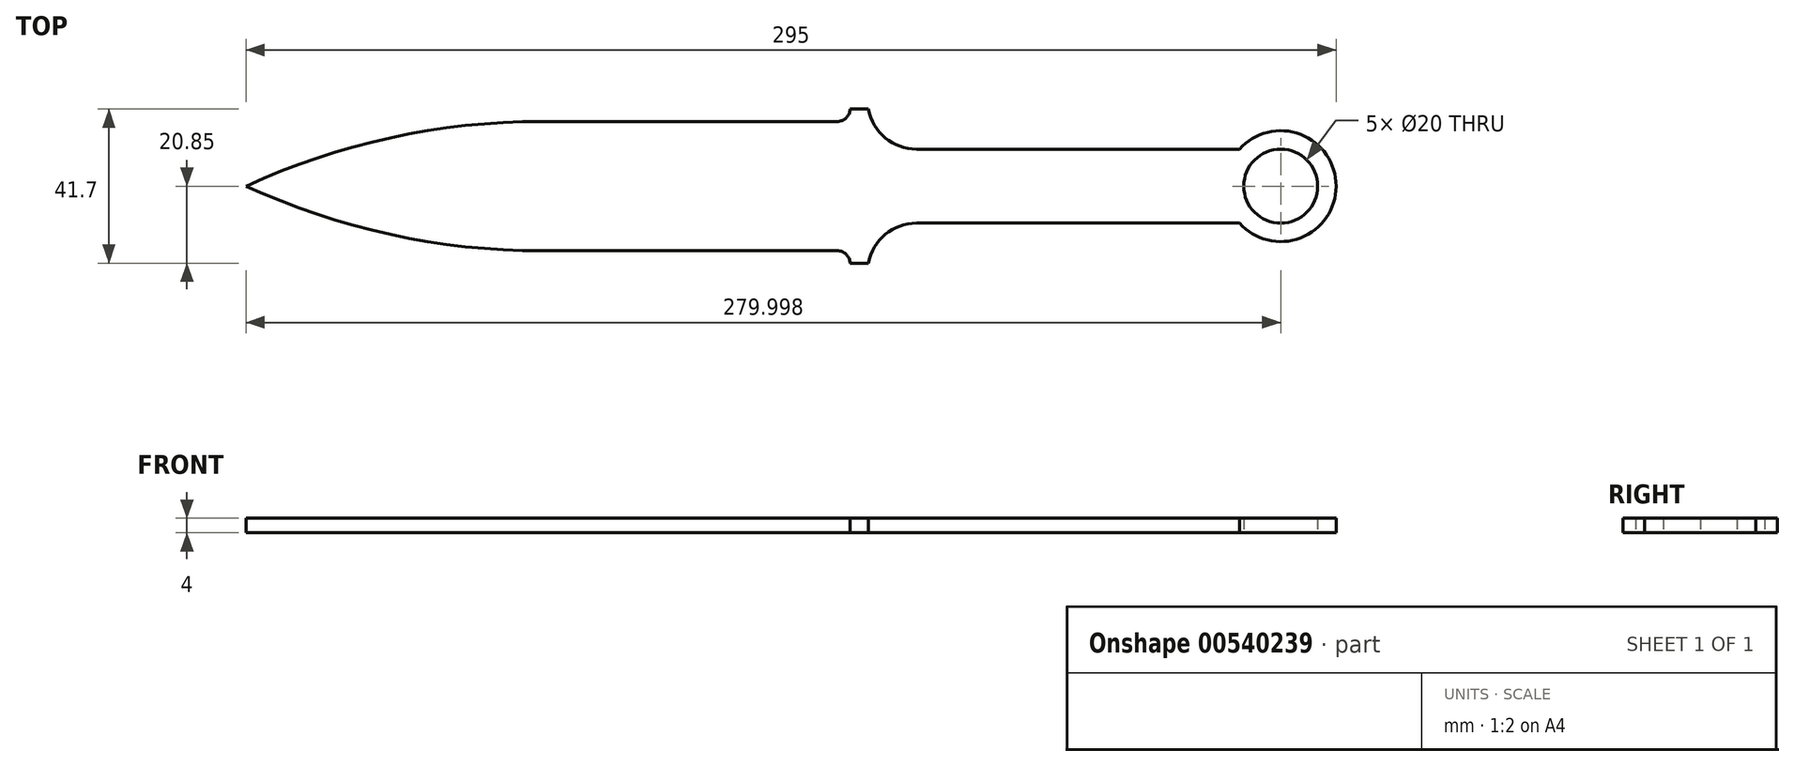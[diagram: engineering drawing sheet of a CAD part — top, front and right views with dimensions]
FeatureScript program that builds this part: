
annotation { "Feature Type Name" : "Feature", "Feature Type Description" : "" }
export const myFeature = defineFeature(function(context is Context, id is Id, definition is map)
    precondition{}
    {
        {
            var Q0;
            Q0=qCreatedBy(makeId("Top.planeOp"),FACE);
            var sketch = newSketch(context, id + "F0", { "sketchPlane" : qUnion([Q0])});
            skLineSegment(sketch, "E0", {"start": v(8.08, 17.5) * mm, "end": v(88.08, 17.5) * mm});
            skPoint(sketch, "E1", {"position": v(-71.92, 0) * mm});
            skArc(sketch, "E2", {"start": v(8.08, 17.5) * mm, "mid": v(-32.87, 13.07) * mm, "end": v(-71.92, 0) * mm});
            skPoint(sketch, "E3", {"position": v(223.08, 0) * mm});
            skArc(sketch, "E4", {"start": v(88.08, 17.5) * mm, "mid": v(90.48, 18.47) * mm, "end": v(91.53, 20.85) * mm});
            skLineSegment(sketch, "E5", {"start": v(91.53, 20.85) * mm, "end": v(96.53, 20.85) * mm});
            skPoint(sketch, "E6", {"position": v(208.08, 0) * mm});
            skCircle(sketch, "E7", {"center": v(208.08, 0) * mm, "radius": 10 * mm});
            skLineSegment(sketch, "E8", {"start": v(196.9, 10) * mm, "end": v(109.54, 10) * mm});
            skArc(sketch, "E9", {"start": v(96.53, 20.85) * mm, "mid": v(101.07, 13.07) * mm, "end": v(109.54, 10) * mm});
            skLineSegment(sketch, "E10.MirrorCS", {"start": v(196.9, -10) * mm, "end": v(109.54, -10) * mm});
            skArc(sketch, "E11.MirrorCS", {"start": v(8.08, -17.5) * mm, "mid": v(-32.87, -13.07) * mm, "end": v(-71.92, 0) * mm});
            skLineSegment(sketch, "E12.MirrorCS", {"start": v(8.08, -17.5) * mm, "end": v(88.08, -17.5) * mm});
            skLineSegment(sketch, "E13.MirrorCS", {"start": v(91.53, -20.85) * mm, "end": v(96.53, -20.85) * mm});
            skArc(sketch, "E14.MirrorCS", {"start": v(88.08, -17.5) * mm, "mid": v(90.48, -18.47) * mm, "end": v(91.53, -20.85) * mm});
            skArc(sketch, "E15.MirrorCS", {"start": v(96.53, -20.85) * mm, "mid": v(101.07, -13.07) * mm, "end": v(109.54, -10) * mm});
            skArc(sketch, "E16", {"start": v(196.9, -10) * mm, "mid": v(223.08, 0) * mm, "end": v(196.9, 10) * mm});
            skSolve(sketch);
        }
        {
            var Q0;
            Q0=makeQuery(id+"F0.imprint","IMPRINT",FACE,{"disambiguationData":[TD([[makeQuery(id+"F0.imprint","IMPRINT",EDGE,{"derivedFrom":sQuery(id+"F0.wireOp",EDGE,"E0")}),-1.0]])]});
            extrude(context, id + "F1", {"entities" : qUnion([Q0]), "depth" : 4 * mm, "offsetDistance" : 25 * mm});
        }
    });
